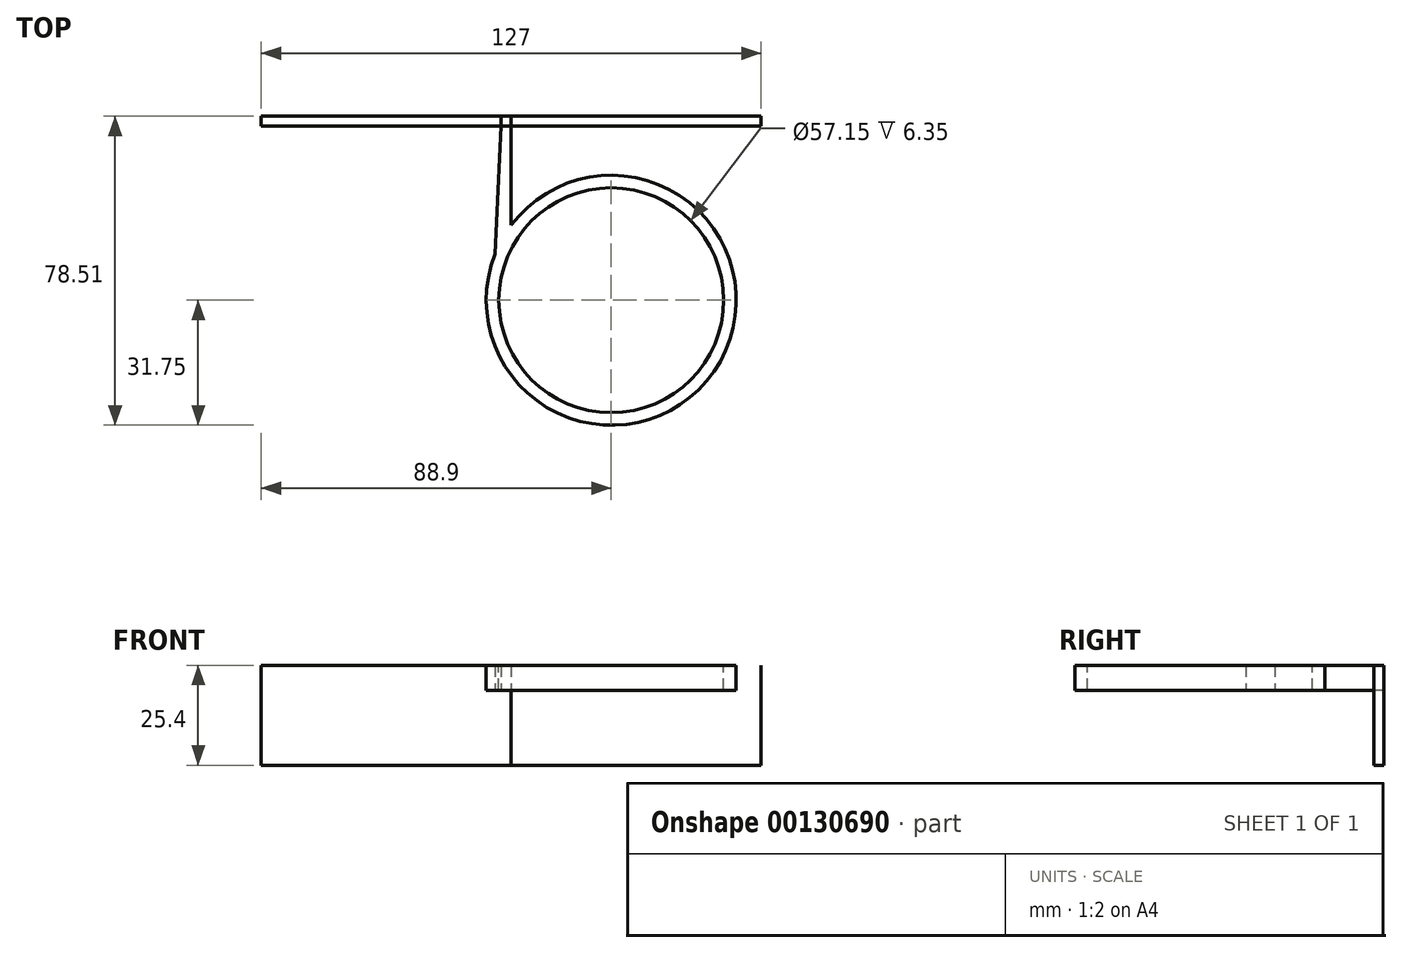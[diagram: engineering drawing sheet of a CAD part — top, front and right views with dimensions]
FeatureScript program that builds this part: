
annotation { "Feature Type Name" : "Feature", "Feature Type Description" : "" }
export const myFeature = defineFeature(function(context is Context, id is Id, definition is map)
    precondition{}
    {
        {
            var Q0;
            Q0=qCreatedBy(makeId("Top.planeOp"),FACE);
            var sketch = newSketch(context, id + "F0", { "sketchPlane" : qUnion([Q0])});
            skCircle(sketch, "E0", {"center": v(0, 0) * mm, "radius": 31.75 * mm});
            skSolve(sketch);
        }
        {
            var Q0;
            Q0=makeQuery(id+"F0.imprint","IMPRINT",FACE,{"disambiguationData":[TD([[makeQuery(id+"F0.imprint","IMPRINT",EDGE,{"derivedFrom":sQuery(id+"F0.wireOp",EDGE,"E0")}),1.0]])]});
            extrude(context, id + "F1", {"entities" : qUnion([Q0]), "depth" : 6.35 * mm});
        }
        {
            var Q0;
            Q0=makeQuery(id+"F1.opExtrude","CAP_FACE",FACE,{"disambiguationData":[OSD([sQuery(id+"F0.wireOp",EDGE,"E0")])],"isStart":false});
            var sketch = newSketch(context, id + "F2", { "sketchPlane" : qUnion([Q0])});
            skCircle(sketch, "E1", {"center": v(0, 0) * mm, "radius": 28.58 * mm});
            skSolve(sketch);
        }
        {
            var Q0;
            Q0=makeQuery(id+"F2.imprint","IMPRINT",FACE,{"disambiguationData":[TD([[makeQuery(id+"F2.imprint","IMPRINT",EDGE,{"derivedFrom":sQuery(id+"F2.wireOp",EDGE,"E1")}),1.0]])]});
            extrude(context, id + "F3", {"entities" : qUnion([Q0]), "operationType" : NewBodyOperationType.REMOVE, "oppositeDirection" : true, "depth" : 25.4 * mm});
        }
        {
            var Q0;
            Q0=qCreatedBy(makeId("Top.planeOp"),FACE);
            var sketch = newSketch(context, id + "F4", { "sketchPlane" : qUnion([Q0])});
            skLineSegment(sketch, "E2.bottom", {"start": v(-25.4, 44.45) * mm, "end": v(25.4, 44.45) * mm});
            skLineSegment(sketch, "E2.top", {"start": v(-25.4, -44.45) * mm, "end": v(25.4, -44.45) * mm});
            skLineSegment(sketch, "E2.left", {"start": v(-25.4, 44.45) * mm, "end": v(-25.4, -44.45) * mm});
            skLineSegment(sketch, "E2.right", {"start": v(25.4, 44.45) * mm, "end": v(25.4, -44.45) * mm});
            skPoint(sketch, "E2.middle", {"position": v(0, 0) * mm});
            skSolve(sketch);
        }
        {
            var Q0;
            Q0=makeQuery(id+"F4.imprint","IMPRINT",FACE,{"disambiguationData":[TD([[makeQuery(id+"F4.imprint","IMPRINT",EDGE,{"derivedFrom":sQuery(id+"F4.wireOp",EDGE,"E2.bottom")}),-1.0]])]});
            var sketch = newSketch(context, id + "F5", { "sketchPlane" : qUnion([Q0])});
            skLineSegment(sketch, "E3", {"start": v(-29.62, 9.4) * mm, "end": v(-19.5, 23.46) * mm});
            skLineSegment(sketch, "E4", {"start": v(-19.5, 23.46) * mm, "end": v(-5.64, 30.15) * mm});
            skLineSegment(sketch, "E5", {"start": v(-5.64, 30.15) * mm, "end": v(6.12, 30.15) * mm});
            skLineSegment(sketch, "E6", {"start": v(6.12, 30.15) * mm, "end": v(20.96, 23.92) * mm});
            skLineSegment(sketch, "E7", {"start": v(20.96, 23.92) * mm, "end": v(27.02, 14.84) * mm});
            skLineSegment(sketch, "E8", {"start": v(27.02, 14.84) * mm, "end": v(31.83, 2.96) * mm});
            skLineSegment(sketch, "E9", {"start": v(31.83, 2.96) * mm, "end": v(31.83, 44.22) * mm});
            skLineSegment(sketch, "E10", {"start": v(31.83, 44.22) * mm, "end": v(-27.96, 44.22) * mm});
            skLineSegment(sketch, "E11", {"start": v(-27.96, 44.22) * mm, "end": v(-29.62, 9.4) * mm});
            skSolve(sketch);
        }
        {
            var Q0;
            {var subQ1=sQuery(id+"F5.wireOp",EDGE,"E3");Q0=makeQuery(id+"F5.imprint","IMPRINT",FACE,{"disambiguationData":[TD([[makeQuery(id+"F5.imprint","IMPRINT",EDGE,{"derivedFrom":subQ1}),1.0]])]});}
            extrude(context, id + "F6", {"entities" : qUnion([Q0]), "operationType" : NewBodyOperationType.ADD, "depth" : 6.35 * mm});
        }
        {
            var Q0;
            Q0=makeQuery(id+"F6.opExtrude","SWEPT_FACE",FACE,{"disambiguationData":[OSD([sQuery(id+"F5.wireOp",EDGE,"E10")])]});
            var sketch = newSketch(context, id + "F7", { "sketchPlane" : qUnion([Q0])});
            skLineSegment(sketch, "E12.bottom", {"start": v(25.4, 6.35) * mm, "end": v(-38.1, 6.35) * mm});
            skLineSegment(sketch, "E12.top", {"start": v(25.4, -19.05) * mm, "end": v(-38.1, -19.05) * mm});
            skLineSegment(sketch, "E12.left", {"start": v(25.4, 6.35) * mm, "end": v(25.4, -19.05) * mm});
            skLineSegment(sketch, "E12.right", {"start": v(-38.1, 6.35) * mm, "end": v(-38.1, -19.05) * mm});
            skSolve(sketch);
        }
        {
            var Q0;
            {var subQ1=sQuery(id+"F7.wireOp",EDGE,"E12.top");Q0=makeQuery(id+"F7.imprint","IMPRINT",FACE,{"disambiguationData":[TD([[makeQuery(id+"F7.imprint","IMPRINT",EDGE,{"derivedFrom":subQ1}),-1.0]])]});}
            extrude(context, id + "F8", {"entities" : qUnion([Q0]), "depth" : 2.54 * mm});
        }
        {
            var Q0;
            Q0=makeQuery(id+"F6.opExtrude","SWEPT_FACE",FACE,{"disambiguationData":[OSD([sQuery(id+"F5.wireOp",EDGE,"E10")])]});
            extrude(context, id + "F9", {"entities" : qUnion([Q0]), "depth" : 2.54 * mm});
        }
        {
            var Q0;
            Q0=makeQuery(id+"F8.opExtrude","CAP_FACE",FACE,{"disambiguationData":[OSD([sQuery(id+"F5.wireOp",EDGE,"E9"),sQuery(id+"F5.wireOp",EDGE,"E10"),sQuery(id+"F7.wireOp",EDGE,"E12.bottom"),sQuery(id+"F7.wireOp",EDGE,"E12.top"),sQuery(id+"F7.wireOp",EDGE,"E12.left"),sQuery(id+"F7.wireOp",EDGE,"E12.right")])],"isStart":false});
            var sketch = newSketch(context, id + "F10", { "sketchPlane" : qUnion([Q0])});
            skLineSegment(sketch, "E13.bottom", {"start": v(25.4, 6.35) * mm, "end": v(88.9, 6.35) * mm});
            skLineSegment(sketch, "E13.top", {"start": v(25.4, -19.05) * mm, "end": v(88.9, -19.05) * mm});
            skLineSegment(sketch, "E13.left", {"start": v(25.4, 6.35) * mm, "end": v(25.4, -19.05) * mm});
            skLineSegment(sketch, "E13.right", {"start": v(88.9, 6.35) * mm, "end": v(88.9, -19.05) * mm});
            skSolve(sketch);
        }
        {
            var Q0;
            {var subQ5=sQuery(id+"F10.wireOp",EDGE,"E13.bottom");Q0=makeQuery(id+"F10.imprint","IMPRINT",FACE,{"disambiguationData":[TD([[makeQuery(id+"F10.imprint","IMPRINT",EDGE,{"derivedFrom":subQ5}),-1.0]])]});}
            extrude(context, id + "F11", {"entities" : qUnion([Q0]), "oppositeDirection" : true, "depth" : 2.54 * mm});
        }
    });
